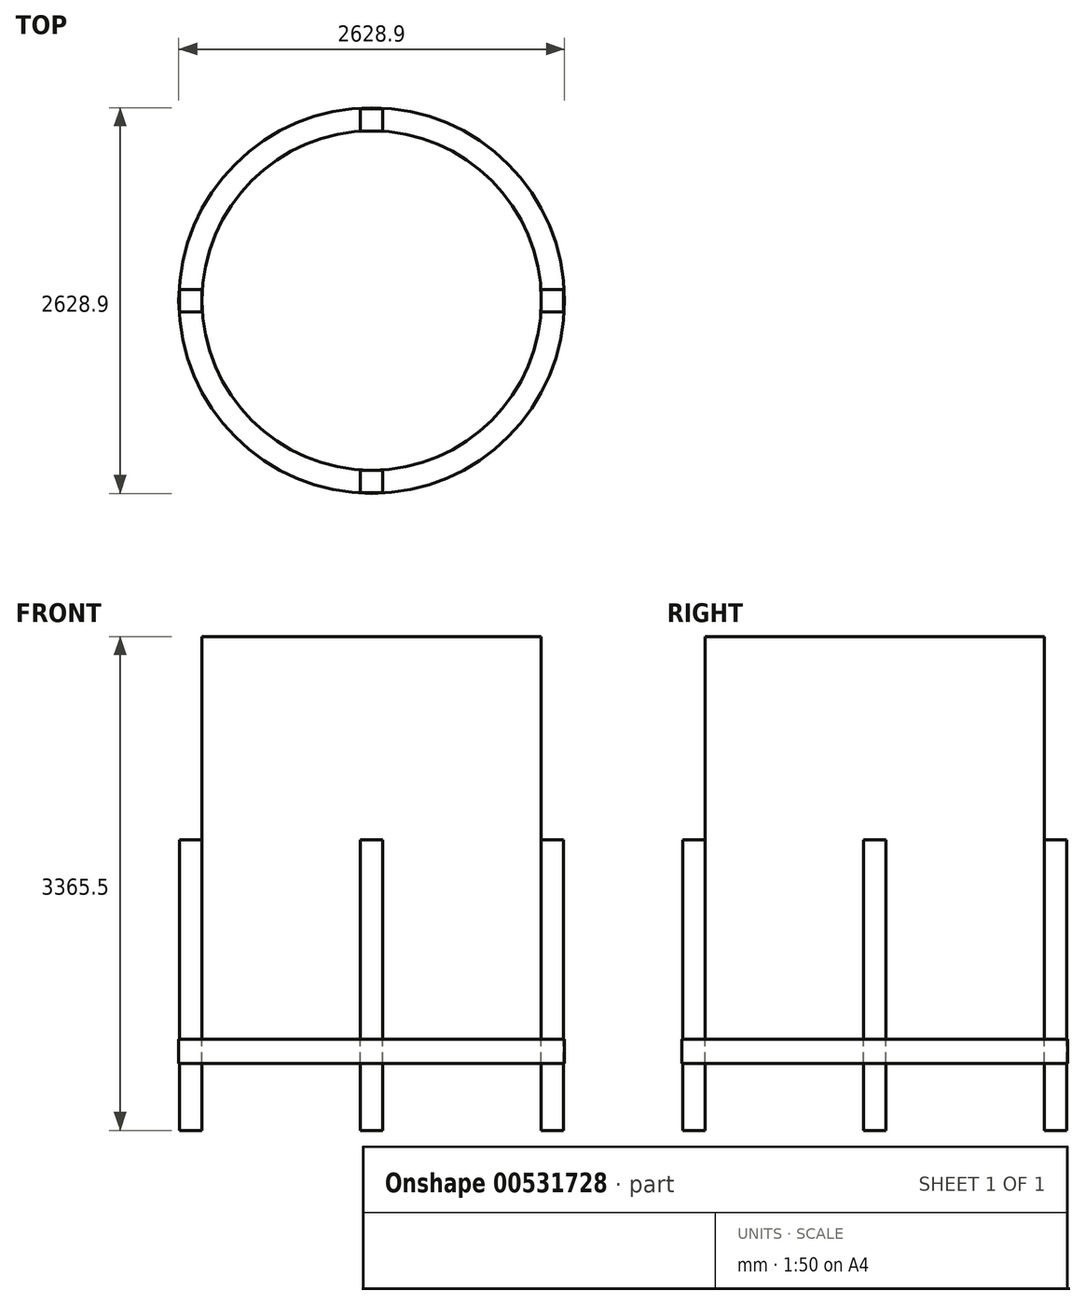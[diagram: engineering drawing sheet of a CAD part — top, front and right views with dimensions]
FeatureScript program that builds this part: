
annotation { "Feature Type Name" : "Feature", "Feature Type Description" : "" }
export const myFeature = defineFeature(function(context is Context, id is Id, definition is map)
    precondition{}
    {
        {
            var Q0;
            Q0=qCreatedBy(makeId("Top.planeOp"),FACE);
            var sketch = newSketch(context, id + "F0", { "sketchPlane" : qUnion([Q0])});
            skCircle(sketch, "E0", {"center": v(0, 0) * mm, "radius": 1155.7 * mm});
            skSolve(sketch);
        }
        {
            var Q0;
            Q0=makeQuery(id+"F0.imprint","IMPRINT",FACE,{"disambiguationData":[TD([[makeQuery(id+"F0.imprint","IMPRINT",EDGE,{"derivedFrom":sQuery(id+"F0.wireOp",EDGE,"E0")}),1.0]])]});
            extrude(context, id + "F1", {"entities" : qUnion([Q0]), "depth" : 2743.2 * mm, "offsetDistance" : 25.4 * mm});
        }
        {
            var Q0;
            Q0=makeQuery(id+"F1.opExtrude","CAP_FACE",FACE,{"disambiguationData":[OSD([sQuery(id+"F0.wireOp",EDGE,"E0")])],"isStart":true});
            var sketch = newSketch(context, id + "F2", { "sketchPlane" : qUnion([Q0])});
            skCircle(sketch, "E1", {"center": v(0, 0) * mm, "radius": 1314.45 * mm});
            skSolve(sketch);
        }
        {
            var Q0;
            Q0=makeQuery(id+"F2.imprint","IMPRINT",FACE,{"disambiguationData":[TD([[makeQuery(id+"F2.imprint","IMPRINT",EDGE,{"derivedFrom":sQuery(id+"F2.wireOp",EDGE,"E1")}),1.0]])]});
            extrude(context, id + "F3", {"entities" : qUnion([Q0]), "depth" : 165.1 * mm, "offsetDistance" : 25.4 * mm});
        }
        {
            var Q0;
            Q0=makeQuery(id+"F3.opExtrude","CAP_FACE",FACE,{"disambiguationData":[OSD([sQuery(id+"F0.wireOp",EDGE,"E0"),sQuery(id+"F2.wireOp",EDGE,"E1")])],"isStart":true});
            var sketch = newSketch(context, id + "F4", { "sketchPlane" : qUnion([Q0])});
            skLineSegment(sketch, "E2.top", {"start": v(-1155.7, 76.2) * mm, "end": v(-1308.1, 76.2) * mm});
            skLineSegment(sketch, "E2.left", {"start": v(-1155.7, 0) * mm, "end": v(-1155.7, 76.2) * mm});
            skLineSegment(sketch, "E2.right", {"start": v(-1308.1, 0) * mm, "end": v(-1308.1, 76.2) * mm});
            skLineSegment(sketch, "E3.top", {"start": v(-1155.7, -76.2) * mm, "end": v(-1308.1, -76.2) * mm});
            skLineSegment(sketch, "E3.left", {"start": v(-1155.7, 0) * mm, "end": v(-1155.7, -76.2) * mm});
            skLineSegment(sketch, "E3.right", {"start": v(-1308.1, 0) * mm, "end": v(-1308.1, -76.2) * mm});
            skLineSegment(sketch, "E4.1.0", {"start": v(76.2, -1155.7) * mm, "end": v(76.2, -1308.1) * mm});
            skLineSegment(sketch, "E4.1.1", {"start": v(0, -1155.7) * mm, "end": v(76.2, -1155.7) * mm});
            skLineSegment(sketch, "E4.1.2", {"start": v(0, -1155.7) * mm, "end": v(-76.2, -1155.7) * mm});
            skLineSegment(sketch, "E4.1.3", {"start": v(-76.2, -1155.7) * mm, "end": v(-76.2, -1308.1) * mm});
            skLineSegment(sketch, "E4.1.4", {"start": v(0, -1308.1) * mm, "end": v(-76.2, -1308.1) * mm});
            skLineSegment(sketch, "E4.1.5", {"start": v(0, -1308.1) * mm, "end": v(76.2, -1308.1) * mm});
            skLineSegment(sketch, "E4.2.0", {"start": v(1155.7, 76.2) * mm, "end": v(1308.1, 76.2) * mm});
            skLineSegment(sketch, "E4.2.1", {"start": v(1155.7, 0) * mm, "end": v(1155.7, 76.2) * mm});
            skLineSegment(sketch, "E4.2.2", {"start": v(1155.7, 0) * mm, "end": v(1155.7, -76.2) * mm});
            skLineSegment(sketch, "E4.2.3", {"start": v(1155.7, -76.2) * mm, "end": v(1308.1, -76.2) * mm});
            skLineSegment(sketch, "E4.2.4", {"start": v(1308.1, 0) * mm, "end": v(1308.1, -76.2) * mm});
            skLineSegment(sketch, "E4.2.5", {"start": v(1308.1, 0) * mm, "end": v(1308.1, 76.2) * mm});
            skLineSegment(sketch, "E4.3.0", {"start": v(-76.2, 1155.7) * mm, "end": v(-76.2, 1308.1) * mm});
            skLineSegment(sketch, "E4.3.1", {"start": v(0, 1155.7) * mm, "end": v(-76.2, 1155.7) * mm});
            skLineSegment(sketch, "E4.3.2", {"start": v(0, 1155.7) * mm, "end": v(76.2, 1155.7) * mm});
            skLineSegment(sketch, "E4.3.3", {"start": v(76.2, 1155.7) * mm, "end": v(76.2, 1308.1) * mm});
            skLineSegment(sketch, "E4.3.4", {"start": v(0, 1308.1) * mm, "end": v(76.2, 1308.1) * mm});
            skLineSegment(sketch, "E4.3.5", {"start": v(0, 1308.1) * mm, "end": v(-76.2, 1308.1) * mm});
            skPoint(sketch, "E4.center", {"position": v(0, 0) * mm});
            skSolve(sketch);
        }
        {
            var Q0;
            Q0 = qSketchRegion(id + "F4", true);
            extrude(context, id + "F5", {"entities" : qUnion([Q0]), "depth" : 1358.9 * mm, "offsetDistance" : 25.4 * mm});
        }
        {
            var Q0;
            Q0 = qSketchRegion(id + "F4", true);
            extrude(context, id + "F6", {"entities" : qUnion([Q0]), "oppositeDirection" : true, "depth" : 622.3 * mm, "offsetDistance" : 25.4 * mm});
        }
    });
